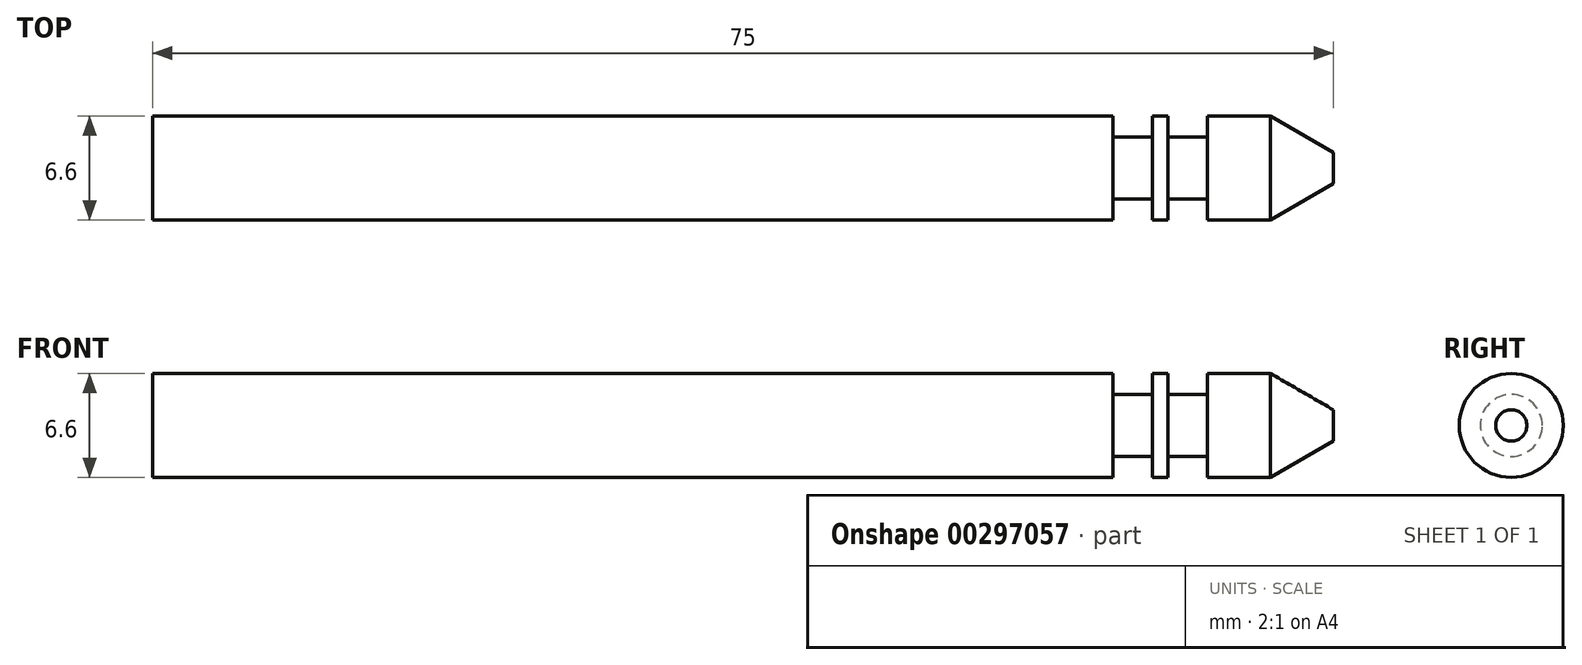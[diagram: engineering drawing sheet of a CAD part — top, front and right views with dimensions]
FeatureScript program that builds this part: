
annotation { "Feature Type Name" : "Feature", "Feature Type Description" : "" }
export const myFeature = defineFeature(function(context is Context, id is Id, definition is map)
    precondition{}
    {
        {
            var Q0;
            Q0=qCreatedBy(makeId("Front.planeOp"),FACE);
            var sketch = newSketch(context, id + "F0", { "sketchPlane" : qUnion([Q0])});
            skLineSegment(sketch, "E0", {"start": v(0, 0) * mm, "end": v(47.46, 0) * mm, "construction": true});
            skLineSegment(sketch, "E1", {"start": v(0, 0) * mm, "end": v(0, 3.3) * mm, "construction": true});
            skLineSegment(sketch, "E2", {"start": v(0, 3.3) * mm, "end": v(12, 3.3) * mm});
            skLineSegment(sketch, "E3", {"start": v(12, 3.3) * mm, "end": v(12, 1.97) * mm});
            skLineSegment(sketch, "E4", {"start": v(12, 1.97) * mm, "end": v(14.5, 1.97) * mm});
            skLineSegment(sketch, "E5", {"start": v(14.5, 1.97) * mm, "end": v(14.5, 3.3) * mm});
            skLineSegment(sketch, "E6", {"start": v(14.5, 3.3) * mm, "end": v(15.5, 3.3) * mm});
            skLineSegment(sketch, "E7", {"start": v(15.5, 3.3) * mm, "end": v(15.5, 1.97) * mm});
            skLineSegment(sketch, "E8", {"start": v(15.5, 1.97) * mm, "end": v(18, 1.97) * mm});
            skLineSegment(sketch, "E9", {"start": v(18, 1.97) * mm, "end": v(18, 3.3) * mm});
            skLineSegment(sketch, "E10", {"start": v(18, 3.3) * mm, "end": v(22, 3.3) * mm});
            skLineSegment(sketch, "E11", {"start": v(22, 3.3) * mm, "end": v(26, 1) * mm});
            skLineSegment(sketch, "E12", {"start": v(26, 1) * mm, "end": v(26, 0) * mm});
            skLineSegment(sketch, "E13", {"start": v(0, 3.3) * mm, "end": v(-49, 3.3) * mm});
            skLineSegment(sketch, "E14", {"start": v(-49, 3.3) * mm, "end": v(-49, 0) * mm});
            skLineSegment(sketch, "E15", {"start": v(-49, 0) * mm, "end": v(26, 0) * mm});
            skSolve(sketch);
        }
        {
            var Q0;
            Q0 = qSketchRegion(id + "F0", true);
            var Q1;
            Q1=sQuery(id+"F0.wireOp",EDGE,"E0");
            revolve(context, id + "F1", {"surfaceOperationType" : NewSurfaceOperationType.NEW, "entities" : qUnion([Q0]), "axis" : qUnion([Q1]), "revolveType" : RevolveType.FULL});
        }
    });
